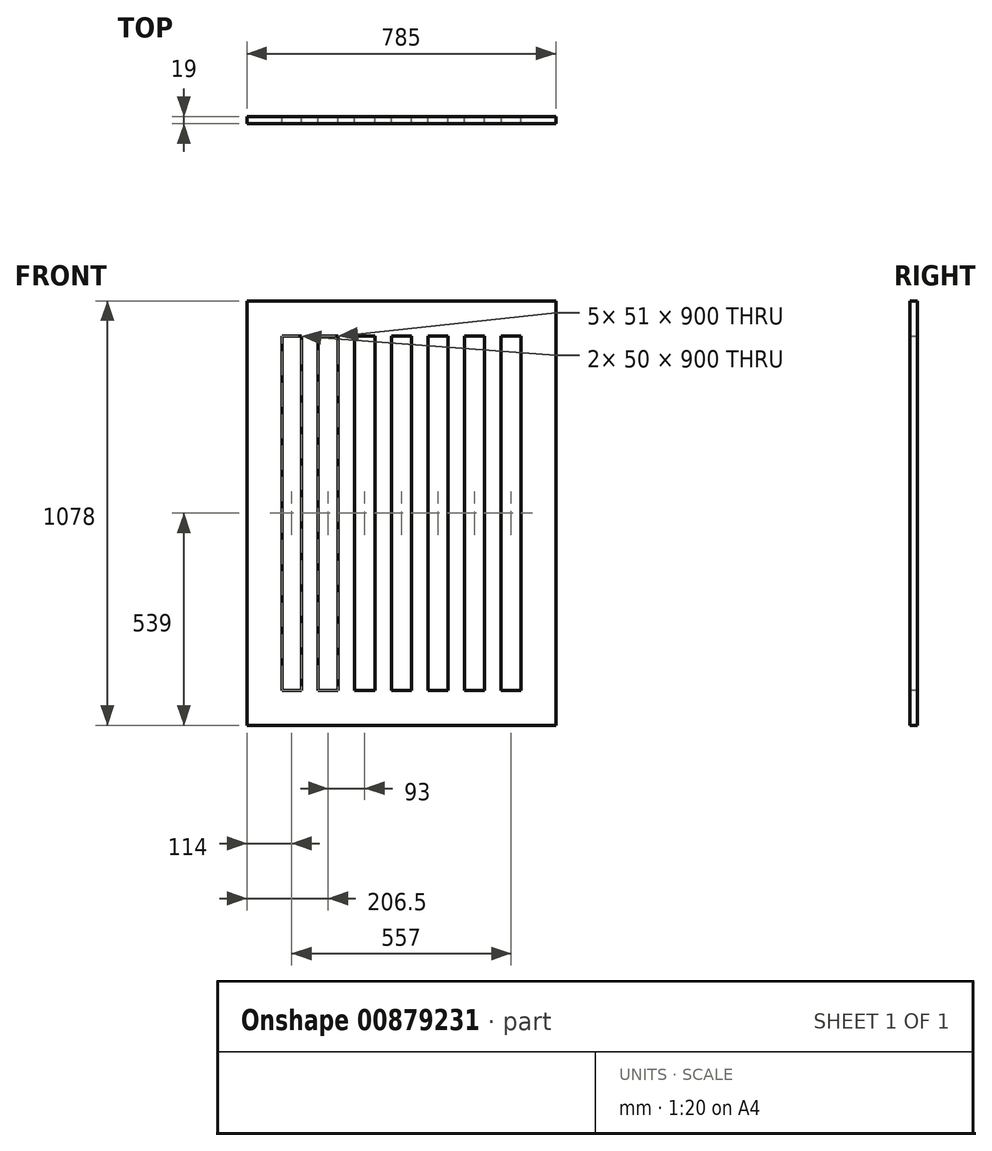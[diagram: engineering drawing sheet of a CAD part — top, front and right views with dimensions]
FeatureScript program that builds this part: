
annotation { "Feature Type Name" : "Feature", "Feature Type Description" : "" }
export const myFeature = defineFeature(function(context is Context, id is Id, definition is map)
    precondition{}
    {
        {
            var Q0;
            Q0=qCreatedBy(makeId("Front.planeOp"),FACE);
            var sketch = newSketch(context, id + "F0", { "sketchPlane" : qUnion([Q0])});
            skLineSegment(sketch, "E0.bottom", {"start": v(-392.5, 539) * mm, "end": v(392.5, 539) * mm});
            skLineSegment(sketch, "E0.top", {"start": v(-392.5, -539) * mm, "end": v(392.5, -539) * mm});
            skLineSegment(sketch, "E0.left", {"start": v(-392.5, 539) * mm, "end": v(-392.5, -539) * mm});
            skLineSegment(sketch, "E0.right", {"start": v(392.5, 539) * mm, "end": v(392.5, -539) * mm});
            skLineSegment(sketch, "E1.bottom", {"start": v(-303.5, 450) * mm, "end": v(303.5, 450) * mm});
            skLineSegment(sketch, "E1.top", {"start": v(-303.5, -450) * mm, "end": v(303.5, -450) * mm});
            skLineSegment(sketch, "E1.left", {"start": v(-303.5, 450) * mm, "end": v(-303.5, -450) * mm});
            skLineSegment(sketch, "E1.right", {"start": v(303.5, 450) * mm, "end": v(303.5, -450) * mm});
            skSolve(sketch);
        }
        {
            var Q0;
            Q0 = qSketchRegion(id + "F0", true);
            extrude(context, id + "F1", {"entities" : qUnion([Q0]), "flatOperationType" : FlatOperationType.REMOVE, "depth" : 19 * mm, "offsetDistance" : 25 * mm, "domain" : OperationDomain.MODEL});
        }
        {
            var Q0;
            Q0=makeQuery(id+"F1.opExtrude","SWEPT_FACE",FACE,{"disambiguationData":[OSD([sQuery(id+"F0.wireOp",EDGE,"E1.bottom")])]});
            var sketch = newSketch(context, id + "F2", { "sketchPlane" : qUnion([Q0])});
            skLineSegment(sketch, "E2.0.2.0", {"start": v(-253.5, 19) * mm, "end": v(-253.5, 0) * mm});
            skLineSegment(sketch, "E2.3.2.0", {"start": v(-253.5, 0) * mm, "end": v(-211.5, 0) * mm});
            skLineSegment(sketch, "E2.6.2.0", {"start": v(-211.5, 19) * mm, "end": v(-211.5, 0) * mm});
            skLineSegment(sketch, "E2.12.2.0", {"start": v(-253.5, 19) * mm, "end": v(-211.5, 19) * mm});
            skLineSegment(sketch, "E3.1.0.0", {"start": v(-160.5, 19) * mm, "end": v(-160.5, 0) * mm});
            skLineSegment(sketch, "E3.1.0.1", {"start": v(-118.5, 19) * mm, "end": v(-118.5, 0) * mm});
            skLineSegment(sketch, "E3.1.0.2", {"start": v(-160.5, 0) * mm, "end": v(-118.5, 0) * mm});
            skLineSegment(sketch, "E3.1.0.3", {"start": v(-160.5, 19) * mm, "end": v(-118.5, 19) * mm});
            skLineSegment(sketch, "E3.2.0.0", {"start": v(-67.5, 19) * mm, "end": v(-67.5, 0) * mm});
            skLineSegment(sketch, "E3.2.0.1", {"start": v(-25.5, 19) * mm, "end": v(-25.5, 0) * mm});
            skLineSegment(sketch, "E3.2.0.2", {"start": v(-67.5, 0) * mm, "end": v(-25.5, 0) * mm});
            skLineSegment(sketch, "E3.2.0.3", {"start": v(-67.5, 19) * mm, "end": v(-25.5, 19) * mm});
            skLineSegment(sketch, "E3.3.0.0", {"start": v(25.5, 19) * mm, "end": v(25.5, 0) * mm});
            skLineSegment(sketch, "E3.3.0.1", {"start": v(67.5, 19) * mm, "end": v(67.5, 0) * mm});
            skLineSegment(sketch, "E3.3.0.2", {"start": v(25.5, 0) * mm, "end": v(67.5, 0) * mm});
            skLineSegment(sketch, "E3.3.0.3", {"start": v(25.5, 19) * mm, "end": v(67.5, 19) * mm});
            skLineSegment(sketch, "E3.4.0.0", {"start": v(118.5, 19) * mm, "end": v(118.5, 0) * mm});
            skLineSegment(sketch, "E3.4.0.1", {"start": v(160.5, 19) * mm, "end": v(160.5, 0) * mm});
            skLineSegment(sketch, "E3.4.0.2", {"start": v(118.5, 0) * mm, "end": v(160.5, 0) * mm});
            skLineSegment(sketch, "E3.4.0.3", {"start": v(118.5, 19) * mm, "end": v(160.5, 19) * mm});
            skLineSegment(sketch, "E3.5.0.0", {"start": v(211.5, 19) * mm, "end": v(211.5, 0) * mm});
            skLineSegment(sketch, "E3.5.0.1", {"start": v(253.5, 19) * mm, "end": v(253.5, 0) * mm});
            skLineSegment(sketch, "E3.5.0.2", {"start": v(211.5, 0) * mm, "end": v(253.5, 0) * mm});
            skLineSegment(sketch, "E3.5.0.3", {"start": v(211.5, 19) * mm, "end": v(253.5, 19) * mm});
            skLineSegment(sketch, "E3.direction1", {"start": v(-253.5, 0) * mm, "end": v(-160.5, 0) * mm, "construction": true});
            skSolve(sketch);
        }
        {
            var Q0;
            Q0 = qSketchRegion(id + "F2", true);
            extrude(context, id + "F3", {"entities" : qUnion([Q0]), "operationType" : NewBodyOperationType.ADD, "flatOperationType" : FlatOperationType.REMOVE, "endBound" : BoundingType.UP_TO_NEXT, "depth" : 25 * mm, "offsetDistance" : 25 * mm, "domain" : OperationDomain.MODEL});
        }
    });
